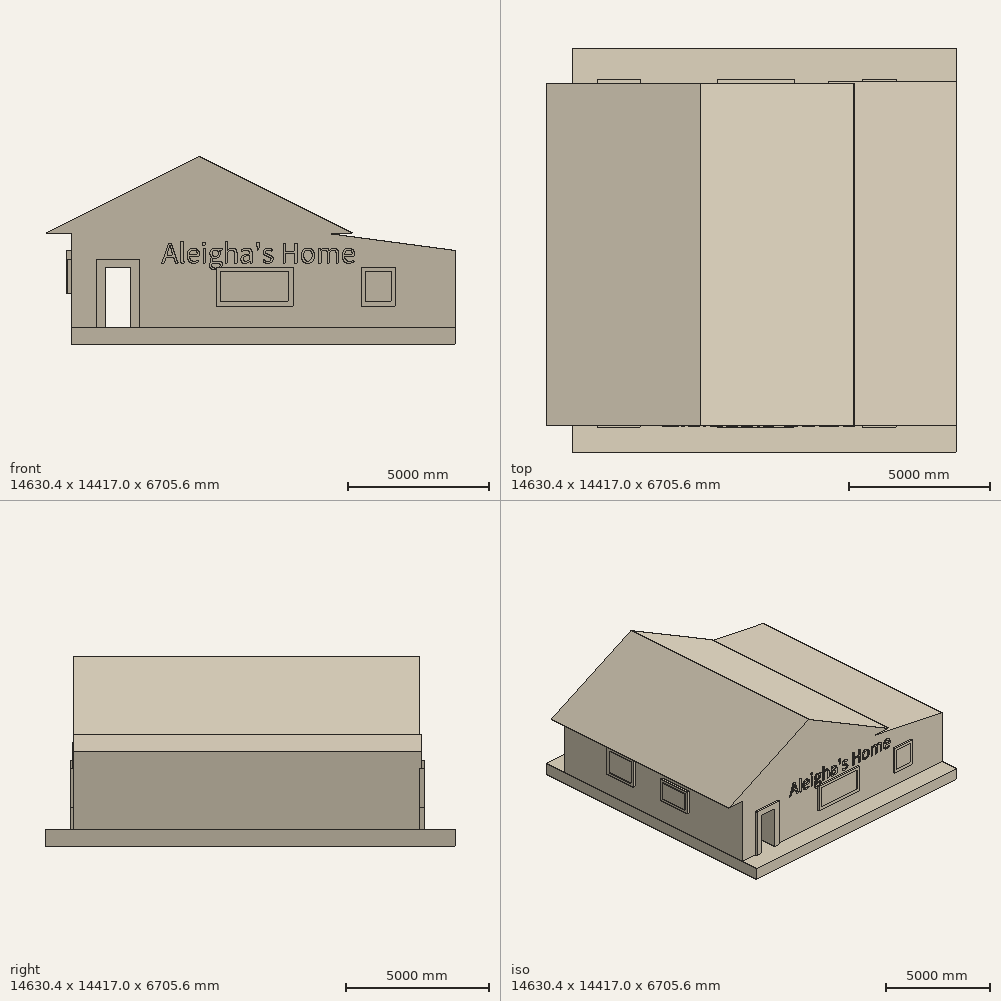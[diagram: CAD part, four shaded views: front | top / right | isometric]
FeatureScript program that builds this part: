
annotation { "Feature Type Name" : "Feature", "Feature Type Description" : "" }
export const myFeature = defineFeature(function(context is Context, id is Id, definition is map)
    precondition{}
    {
        {
            var Q0;
            Q0=qCreatedBy(makeId("Front.planeOp"),FACE);
            var sketch = newSketch(context, id + "F0", { "sketchPlane" : qUnion([Q0])});
            skLineSegment(sketch, "E0", {"start": v(0, 0) * mm, "end": v(-4572, 0) * mm});
            skLineSegment(sketch, "E1", {"start": v(0, 0) * mm, "end": v(4572, 0) * mm});
            skLineSegment(sketch, "E2", {"start": v(0, 0) * mm, "end": v(0, 2286) * mm});
            skLineSegment(sketch, "E3", {"start": v(-4572, 0) * mm, "end": v(-5486.4, 0) * mm});
            skLineSegment(sketch, "E4", {"start": v(4572, 0) * mm, "end": v(5486.4, 0) * mm});
            skLineSegment(sketch, "E5", {"start": v(4572, 0) * mm, "end": v(0, 2286) * mm});
            skLineSegment(sketch, "E6", {"start": v(-4572, 0) * mm, "end": v(0, 2286) * mm});
            skLineSegment(sketch, "E7", {"start": v(-4572, 0) * mm, "end": v(-4572, -3352.8) * mm});
            skLineSegment(sketch, "E8", {"start": v(-4572, -3352.8) * mm, "end": v(-4572, -3962.4) * mm});
            skLineSegment(sketch, "E9", {"start": v(4572, 0) * mm, "end": v(4572, -3352.8) * mm});
            skLineSegment(sketch, "E10", {"start": v(4572, -3352.8) * mm, "end": v(4572, -3962.4) * mm});
            skLineSegment(sketch, "E11", {"start": v(-4572, -3962.4) * mm, "end": v(4572, -3962.4) * mm});
            skLineSegment(sketch, "E12", {"start": v(0, 2286) * mm, "end": v(0, 2743.2) * mm});
            skLineSegment(sketch, "E13", {"start": v(-5486.4, 0) * mm, "end": v(0, 2743.2) * mm});
            skLineSegment(sketch, "E14", {"start": v(5486.4, 0) * mm, "end": v(0, 2743.2) * mm});
            skLineSegment(sketch, "E15", {"start": v(4572, -3962.4) * mm, "end": v(9144, -3962.4) * mm});
            skLineSegment(sketch, "E16", {"start": v(4572, -3352.8) * mm, "end": v(9144, -3352.8) * mm});
            skLineSegment(sketch, "E17", {"start": v(9144, -3352.8) * mm, "end": v(9144, -3962.4) * mm});
            skLineSegment(sketch, "E18", {"start": v(9144, -3352.8) * mm, "end": v(9144, -609.6) * mm});
            skLineSegment(sketch, "E19", {"start": v(-4572, -3352.8) * mm, "end": v(4572, -3352.8) * mm});
            skLineSegment(sketch, "E20.bottom", {"start": v(-3352.8, -3352.8) * mm, "end": v(-2438.4, -3352.8) * mm});
            skLineSegment(sketch, "E20.top", {"start": v(-3352.8, -1219.2) * mm, "end": v(-2438.4, -1219.2) * mm});
            skLineSegment(sketch, "E20.left", {"start": v(-3352.8, -3352.8) * mm, "end": v(-3352.8, -1219.2) * mm});
            skLineSegment(sketch, "E20.right", {"start": v(-2438.4, -3352.8) * mm, "end": v(-2438.4, -1219.2) * mm});
            skLineSegment(sketch, "E21.0", {"start": v(-2133.6, -3352.8) * mm, "end": v(-2133.6, -914.4) * mm});
            skLineSegment(sketch, "E21.1", {"start": v(-3657.6, -914.4) * mm, "end": v(-2133.6, -914.4) * mm});
            skLineSegment(sketch, "E21.2", {"start": v(-3657.6, -3352.8) * mm, "end": v(-3657.6, -914.4) * mm});
            skLineSegment(sketch, "E22.bottom", {"start": v(609.6, -1219.2) * mm, "end": v(3352.8, -1219.2) * mm});
            skLineSegment(sketch, "E22.top", {"start": v(609.6, -2590.8) * mm, "end": v(3352.8, -2590.8) * mm});
            skLineSegment(sketch, "E22.left", {"start": v(609.6, -1219.2) * mm, "end": v(609.6, -2590.8) * mm});
            skLineSegment(sketch, "E22.right", {"start": v(3352.8, -1219.2) * mm, "end": v(3352.8, -2590.8) * mm});
            skLineSegment(sketch, "E23.0", {"start": v(762, -1371.6) * mm, "end": v(762, -2438.4) * mm});
            skLineSegment(sketch, "E23.1", {"start": v(762, -1371.6) * mm, "end": v(3200.4, -1371.6) * mm});
            skLineSegment(sketch, "E23.2", {"start": v(3200.4, -1371.6) * mm, "end": v(3200.4, -2438.4) * mm});
            skLineSegment(sketch, "E23.3", {"start": v(762, -2438.4) * mm, "end": v(3200.4, -2438.4) * mm});
            skLineSegment(sketch, "E24", {"start": v(4572, 0) * mm, "end": v(9144, -609.6) * mm});
            skLineSegment(sketch, "E25", {"start": v(4572, -615.97) * mm, "end": v(9144, -1219.2) * mm});
            skLineSegment(sketch, "E26.bottom", {"start": v(5791.2, -1219.2) * mm, "end": v(7010.4, -1219.2) * mm});
            skLineSegment(sketch, "E26.top", {"start": v(5791.2, -2590.8) * mm, "end": v(7010.4, -2590.8) * mm});
            skLineSegment(sketch, "E26.left", {"start": v(5791.2, -1219.2) * mm, "end": v(5791.2, -2590.8) * mm});
            skLineSegment(sketch, "E26.right", {"start": v(7010.4, -1219.2) * mm, "end": v(7010.4, -2590.8) * mm});
            skLineSegment(sketch, "E27.0", {"start": v(5943.6, -1371.6) * mm, "end": v(6858, -1371.6) * mm});
            skLineSegment(sketch, "E27.1", {"start": v(5943.6, -1371.6) * mm, "end": v(5943.6, -2438.4) * mm});
            skLineSegment(sketch, "E27.2", {"start": v(5943.6, -2438.4) * mm, "end": v(6858, -2438.4) * mm});
            skLineSegment(sketch, "E27.3", {"start": v(6858, -1371.6) * mm, "end": v(6858, -2438.4) * mm});
            skSolve(sketch);
        }
        {
            var Q0;
            Q0=makeQuery(id+"F0.imprint","IMPRINT",FACE,{"disambiguationData":[TD([[makeQuery(id+"F0.imprint","IMPRINT",EDGE,{"derivedFrom":sQuery(id+"F0.wireOp",EDGE,"E3")}),-1.0]])]});
            var Q1;
            Q1=makeQuery(id+"F0.imprint","IMPRINT",FACE,{"disambiguationData":[TD([[makeQuery(id+"F0.imprint","IMPRINT",EDGE,{"derivedFrom":sQuery(id+"F0.wireOp",EDGE,"E4")}),1.0]])]});
            extrude(context, id + "F1", {"entities" : qUnion([Q0, Q1]), "depth" : 12192 * mm, "offsetDistance" : 30.48 * mm});
        }
        {
            var Q0;
            Q0=makeQuery(id+"F0.imprint","IMPRINT",FACE,{"disambiguationData":[TD([[makeQuery(id+"F0.imprint","IMPRINT",EDGE,{"derivedFrom":sQuery(id+"F0.wireOp",EDGE,"E0")}),1.0]])]});
            var Q1;
            {var subQ2=sQuery(id+"F0.wireOp",EDGE,"E16");Q1=makeQuery(id+"F0.imprint","IMPRINT",FACE,{"disambiguationData":[TD([[makeQuery(id+"F0.imprint","IMPRINT",EDGE,{"derivedFrom":subQ2}),1.0]])]});}
            extrude(context, id + "F2", {"entities" : qUnion([Q0, Q1]), "depth" : 12192 * mm, "offsetDistance" : 30.48 * mm});
        }
        {
            var Q0;
            Q0=makeQuery(id+"F0.imprint","IMPRINT",FACE,{"disambiguationData":[TD([[makeQuery(id+"F0.imprint","IMPRINT",EDGE,{"derivedFrom":sQuery(id+"F0.wireOp",EDGE,"E0")}),-1.0]])]});
            var Q1;
            Q1=makeQuery(id+"F0.imprint","IMPRINT",FACE,{"disambiguationData":[TD([[makeQuery(id+"F0.imprint","IMPRINT",EDGE,{"derivedFrom":sQuery(id+"F0.wireOp",EDGE,"E1")}),1.0]])]});
            extrude(context, id + "F3", {"entities" : qUnion([Q0, Q1]), "depth" : 12192 * mm, "offsetDistance" : 30.48 * mm});
        }
        {
            var Q0;
            Q0=makeQuery(id+"F0.imprint","IMPRINT",FACE,{"disambiguationData":[TD([[makeQuery(id+"F0.imprint","IMPRINT",EDGE,{"derivedFrom":sQuery(id+"F0.wireOp",EDGE,"E20.top")}),1.0]])]});
            var Q1;
            Q1=makeQuery(id+"F0.imprint","IMPRINT",FACE,{"disambiguationData":[TD([[makeQuery(id+"F0.imprint","IMPRINT",EDGE,{"derivedFrom":sQuery(id+"F0.wireOp",EDGE,"E22.bottom")}),-1.0]])]});
            var Q2;
            Q2=makeQuery(id+"F0.imprint","IMPRINT",FACE,{"disambiguationData":[TD([[makeQuery(id+"F0.imprint","IMPRINT",EDGE,{"derivedFrom":sQuery(id+"F0.wireOp",EDGE,"E26.bottom")}),-1.0]])]});
            extrude(context, id + "F4", {"entities" : qUnion([Q0, Q1, Q2]), "depth" : 12283.44 * mm, "offsetDistance" : 30.48 * mm, "hasSecondDirection" : true, "secondDirectionOppositeDirection" : true, "secondDirectionDepth" : 152.4 * mm});
        }
        {
            var Q0;
            Q0=makeQuery(id+"F0.imprint","IMPRINT",FACE,{"disambiguationData":[TD([[makeQuery(id+"F0.imprint","IMPRINT",EDGE,{"derivedFrom":sQuery(id+"F0.wireOp",EDGE,"E20.bottom")}),1.0]])]});
            var Q1;
            Q1=makeQuery(id+"F0.imprint","IMPRINT",FACE,{"disambiguationData":[TD([[makeQuery(id+"F0.imprint","IMPRINT",EDGE,{"derivedFrom":sQuery(id+"F0.wireOp",EDGE,"E23.0")}),1.0]])]});
            var Q2;
            Q2=makeQuery(id+"F0.imprint","IMPRINT",FACE,{"disambiguationData":[TD([[makeQuery(id+"F0.imprint","IMPRINT",EDGE,{"derivedFrom":sQuery(id+"F0.wireOp",EDGE,"E27.0")}),-1.0]])]});
            extrude(context, id + "F5", {"entities" : qUnion([Q0, Q1, Q2]), "depth" : 12283.44 * mm, "offsetDistance" : 30.48 * mm, "hasSecondDirection" : true, "secondDirectionOppositeDirection" : true, "secondDirectionDepth" : 152.4 * mm});
        }
        {
            var Q0;
            Q0=makeQuery(id+"F2.opExtrude","SWEPT_FACE",FACE,{"disambiguationData":[OSD([sQuery(id+"F0.wireOp",EDGE,"E7")])]});
            var sketch = newSketch(context, id + "F6", { "sketchPlane" : qUnion([Q0])});
            skLineSegment(sketch, "E28.bottom", {"start": v(3048, -609.6) * mm, "end": v(4876.8, -609.6) * mm});
            skLineSegment(sketch, "E28.top", {"start": v(3048, -2133.6) * mm, "end": v(4876.8, -2133.6) * mm});
            skLineSegment(sketch, "E28.left", {"start": v(3048, -609.6) * mm, "end": v(3048, -2133.6) * mm});
            skLineSegment(sketch, "E28.right", {"start": v(4876.8, -609.6) * mm, "end": v(4876.8, -2133.6) * mm});
            skLineSegment(sketch, "E29.0", {"start": v(3200.4, -762) * mm, "end": v(3200.4, -1981.2) * mm});
            skLineSegment(sketch, "E29.1", {"start": v(3200.4, -762) * mm, "end": v(4724.4, -762) * mm});
            skLineSegment(sketch, "E29.2", {"start": v(4724.4, -762) * mm, "end": v(4724.4, -1981.2) * mm});
            skLineSegment(sketch, "E29.3", {"start": v(3200.4, -1981.2) * mm, "end": v(4724.4, -1981.2) * mm});
            skLineSegment(sketch, "E30.bottom", {"start": v(6705.6, -914.4) * mm, "end": v(8534.4, -914.4) * mm});
            skLineSegment(sketch, "E30.top", {"start": v(6705.6, -2133.6) * mm, "end": v(8534.4, -2133.6) * mm});
            skLineSegment(sketch, "E30.left", {"start": v(6705.6, -914.4) * mm, "end": v(6705.6, -2133.6) * mm});
            skLineSegment(sketch, "E30.right", {"start": v(8534.4, -914.4) * mm, "end": v(8534.4, -2133.6) * mm});
            skLineSegment(sketch, "E31.0", {"start": v(6858, -1066.8) * mm, "end": v(8382, -1066.8) * mm});
            skLineSegment(sketch, "E31.1", {"start": v(6858, -1066.8) * mm, "end": v(6858, -1981.2) * mm});
            skLineSegment(sketch, "E31.2", {"start": v(6858, -1981.2) * mm, "end": v(8382, -1981.2) * mm});
            skLineSegment(sketch, "E31.3", {"start": v(8382, -1066.8) * mm, "end": v(8382, -1981.2) * mm});
            skSolve(sketch);
        }
        {
            var Q0;
            Q0=makeQuery(id+"F6.imprint","IMPRINT",FACE,{"disambiguationData":[TD([[makeQuery(id+"F6.imprint","IMPRINT",EDGE,{"derivedFrom":sQuery(id+"F6.wireOp",EDGE,"E28.bottom")}),-1.0]])]});
            extrude(context, id + "F7", {"entities" : qUnion([Q0]), "operationType" : NewBodyOperationType.ADD, "oppositeDirection" : true, "depth" : 67.06 * mm, "offsetDistance" : 30.48 * mm, "hasSecondDirection" : true, "secondDirectionOppositeDirection" : false, "secondDirectionDepth" : 152.4 * mm});
        }
        {
            var Q0;
            {var subQ0=sQuery(id+"F0.wireOp",EDGE,"E24");Q0=makeQuery(id+"F0.imprint","IMPRINT",FACE,{"disambiguationData":[TD([[makeQuery(id+"F0.imprint","IMPRINT",EDGE,{"derivedFrom":subQ0}),-1.0]])]});}
            extrude(context, id + "F8", {"entities" : qUnion([Q0]), "operationType" : NewBodyOperationType.ADD, "depth" : 30.48 * mm, "offsetDistance" : 30.48 * mm});
        }
        {
            var Q0;
            {var subQ3=sQuery(id+"F0.wireOp",EDGE,"E8");Q0=makeQuery(id+"F0.imprint","IMPRINT",FACE,{"disambiguationData":[TD([[makeQuery(id+"F0.imprint","IMPRINT",EDGE,{"derivedFrom":subQ3}),1.0]])]});}
            var Q1;
            Q1=makeQuery(id+"F0.imprint","IMPRINT",FACE,{"disambiguationData":[TD([[makeQuery(id+"F0.imprint","IMPRINT",EDGE,{"derivedFrom":sQuery(id+"F0.wireOp",EDGE,"E10")}),1.0]])]});
            extrude(context, id + "F9", {"entities" : qUnion([Q0, Q1]), "depth" : 13167.36 * mm, "offsetDistance" : 30.48 * mm, "hasSecondDirection" : true, "secondDirectionOppositeDirection" : true, "secondDirectionDepth" : 1249.68 * mm});
        }
        {
            var Q0;
            {var subQ0=sQuery(id+"F0.wireOp",EDGE,"E24");Q0=makeQuery(id+"F0.imprint","IMPRINT",FACE,{"disambiguationData":[TD([[makeQuery(id+"F0.imprint","IMPRINT",EDGE,{"derivedFrom":subQ0}),-1.0]])]});}
            extrude(context, id + "F10", {"entities" : qUnion([Q0]), "operationType" : NewBodyOperationType.ADD, "depth" : 12192 * mm, "offsetDistance" : 30.48 * mm, "hasSecondDirection" : true, "secondDirectionOppositeDirection" : true, "secondDirectionDepth" : 60.96 * mm});
        }
        {
            var Q0;
            Q0=makeQuery(id+"F3.opExtrude","CAP_FACE",FACE,{"disambiguationData":[OSD([sQuery(id+"F0.wireOp",EDGE,"E0"),sQuery(id+"F0.wireOp",EDGE,"E1"),sQuery(id+"F0.wireOp",EDGE,"E5"),sQuery(id+"F0.wireOp",EDGE,"E6")])],"isStart":false});
            var sketch = newSketch(context, id + "F11", { "sketchPlane" : qUnion([Q0])});
            skText(sketch, "E32", { "text": "Aleigha\'s Home", "fontName": "NotoSansCJKjp-Regular.otf"});
            const initialGuessF11  = {"E32": [-1.3343, -1.05958, 1, 0, 0.6882]};
            skSetInitialGuess(sketch, initialGuessF11);
            skSolve(sketch);
        }
        {
            var Q0;
            Q0=makeQuery(id+"F11.imprint","IMPRINT",FACE,{"disambiguationData":[TD([[makeQuery(id+"F11.imprint","IMPRINT",EDGE,{"derivedFrom":sQuery(id+"F11.wireOp",EDGE,"E32.sketch_text.stroke-34")}),1.0]])]});
            var Q1;
            Q1=makeQuery(id+"F11.imprint","IMPRINT",FACE,{"disambiguationData":[TD([[makeQuery(id+"F11.imprint","IMPRINT",EDGE,{"derivedFrom":sQuery(id+"F11.wireOp",EDGE,"E32.sketch_text.stroke-22")}),1.0]])]});
            var Q2;
            Q2=makeQuery(id+"F11.imprint","IMPRINT",FACE,{"disambiguationData":[TD([[makeQuery(id+"F11.imprint","IMPRINT",EDGE,{"derivedFrom":sQuery(id+"F11.wireOp",EDGE,"E32.sketch_text.stroke-14")}),1.0]])]});
            var Q3;
            Q3=makeQuery(id+"F11.imprint","IMPRINT",FACE,{"disambiguationData":[TD([[makeQuery(id+"F11.imprint","IMPRINT",EDGE,{"derivedFrom":sQuery(id+"F11.wireOp",EDGE,"E32.sketch_text.stroke-0")}),1.0]])]});
            var Q4;
            Q4=makeQuery(id+"F11.imprint","IMPRINT",FACE,{"disambiguationData":[TD([[makeQuery(id+"F11.imprint","IMPRINT",EDGE,{"derivedFrom":sQuery(id+"F11.wireOp",EDGE,"E32.sketch_text.stroke-72")}),1.0]])]});
            var Q5;
            Q5=makeQuery(id+"F11.imprint","IMPRINT",FACE,{"disambiguationData":[TD([[makeQuery(id+"F11.imprint","IMPRINT",EDGE,{"derivedFrom":sQuery(id+"F11.wireOp",EDGE,"E32.sketch_text.stroke-42")}),1.0]])]});
            var Q6;
            Q6=makeQuery(id+"F11.imprint","IMPRINT",FACE,{"disambiguationData":[TD([[makeQuery(id+"F11.imprint","IMPRINT",EDGE,{"derivedFrom":sQuery(id+"F11.wireOp",EDGE,"E32.sketch_text.stroke-38")}),1.0]])]});
            var Q7;
            Q7=makeQuery(id+"F11.imprint","IMPRINT",FACE,{"disambiguationData":[TD([[makeQuery(id+"F11.imprint","IMPRINT",EDGE,{"derivedFrom":sQuery(id+"F11.wireOp",EDGE,"E32.sketch_text.stroke-85")}),1.0]])]});
            var Q8;
            Q8=makeQuery(id+"F11.imprint","IMPRINT",FACE,{"disambiguationData":[TD([[makeQuery(id+"F11.imprint","IMPRINT",EDGE,{"derivedFrom":sQuery(id+"F11.wireOp",EDGE,"E32.sketch_text.stroke-101")}),1.0]])]});
            var Q9;
            Q9=makeQuery(id+"F11.imprint","IMPRINT",FACE,{"disambiguationData":[TD([[makeQuery(id+"F11.imprint","IMPRINT",EDGE,{"derivedFrom":sQuery(id+"F11.wireOp",EDGE,"E32.sketch_text.stroke-107")}),1.0]])]});
            var Q10;
            Q10=makeQuery(id+"F11.imprint","IMPRINT",FACE,{"disambiguationData":[TD([[makeQuery(id+"F11.imprint","IMPRINT",EDGE,{"derivedFrom":sQuery(id+"F11.wireOp",EDGE,"E32.sketch_text.stroke-121")}),1.0]])]});
            var Q11;
            Q11=makeQuery(id+"F11.imprint","IMPRINT",FACE,{"disambiguationData":[TD([[makeQuery(id+"F11.imprint","IMPRINT",EDGE,{"derivedFrom":sQuery(id+"F11.wireOp",EDGE,"E32.sketch_text.stroke-133")}),1.0]])]});
            var Q12;
            Q12=makeQuery(id+"F11.imprint","IMPRINT",FACE,{"disambiguationData":[TD([[makeQuery(id+"F11.imprint","IMPRINT",EDGE,{"derivedFrom":sQuery(id+"F11.wireOp",EDGE,"E32.sketch_text.stroke-141")}),1.0]])]});
            var Q13;
            Q13=makeQuery(id+"F11.imprint","IMPRINT",FACE,{"disambiguationData":[TD([[makeQuery(id+"F11.imprint","IMPRINT",EDGE,{"derivedFrom":sQuery(id+"F11.wireOp",EDGE,"E32.sketch_text.stroke-161")}),1.0]])]});
            extrude(context, id + "F12", {"entities" : qUnion([Q0, Q1, Q2, Q3, Q4, Q5, Q6, Q7, Q8, Q9, Q10, Q11, Q12, Q13]), "depth" : 30.48 * mm, "offsetDistance" : 30.48 * mm, "hasSecondDirection" : true, "secondDirectionOppositeDirection" : true, "secondDirectionDepth" : 30.48 * mm});
        }
        {
            var Q0;
            Q0=makeQuery(id+"F6.imprint","IMPRINT",FACE,{"disambiguationData":[TD([[makeQuery(id+"F6.imprint","IMPRINT",EDGE,{"derivedFrom":sQuery(id+"F6.wireOp",EDGE,"E30.bottom")}),-1.0]])]});
            extrude(context, id + "F13", {"entities" : qUnion([Q0]), "operationType" : NewBodyOperationType.ADD, "depth" : 124.97 * mm, "offsetDistance" : 30.48 * mm});
        }
        {
            var Q0;
            Q0=makeQuery(id+"F6.imprint","IMPRINT",FACE,{"disambiguationData":[TD([[makeQuery(id+"F6.imprint","IMPRINT",EDGE,{"derivedFrom":sQuery(id+"F6.wireOp",EDGE,"E29.0")}),1.0]])]});
            var Q1;
            Q1=makeQuery(id+"F6.imprint","IMPRINT",FACE,{"disambiguationData":[TD([[makeQuery(id+"F6.imprint","IMPRINT",EDGE,{"derivedFrom":sQuery(id+"F6.wireOp",EDGE,"E31.0")}),-1.0]])]});
            extrude(context, id + "F14", {"entities" : qUnion([Q0, Q1]), "operationType" : NewBodyOperationType.ADD, "depth" : 134.11 * mm, "offsetDistance" : 30.48 * mm});
        }
    });
